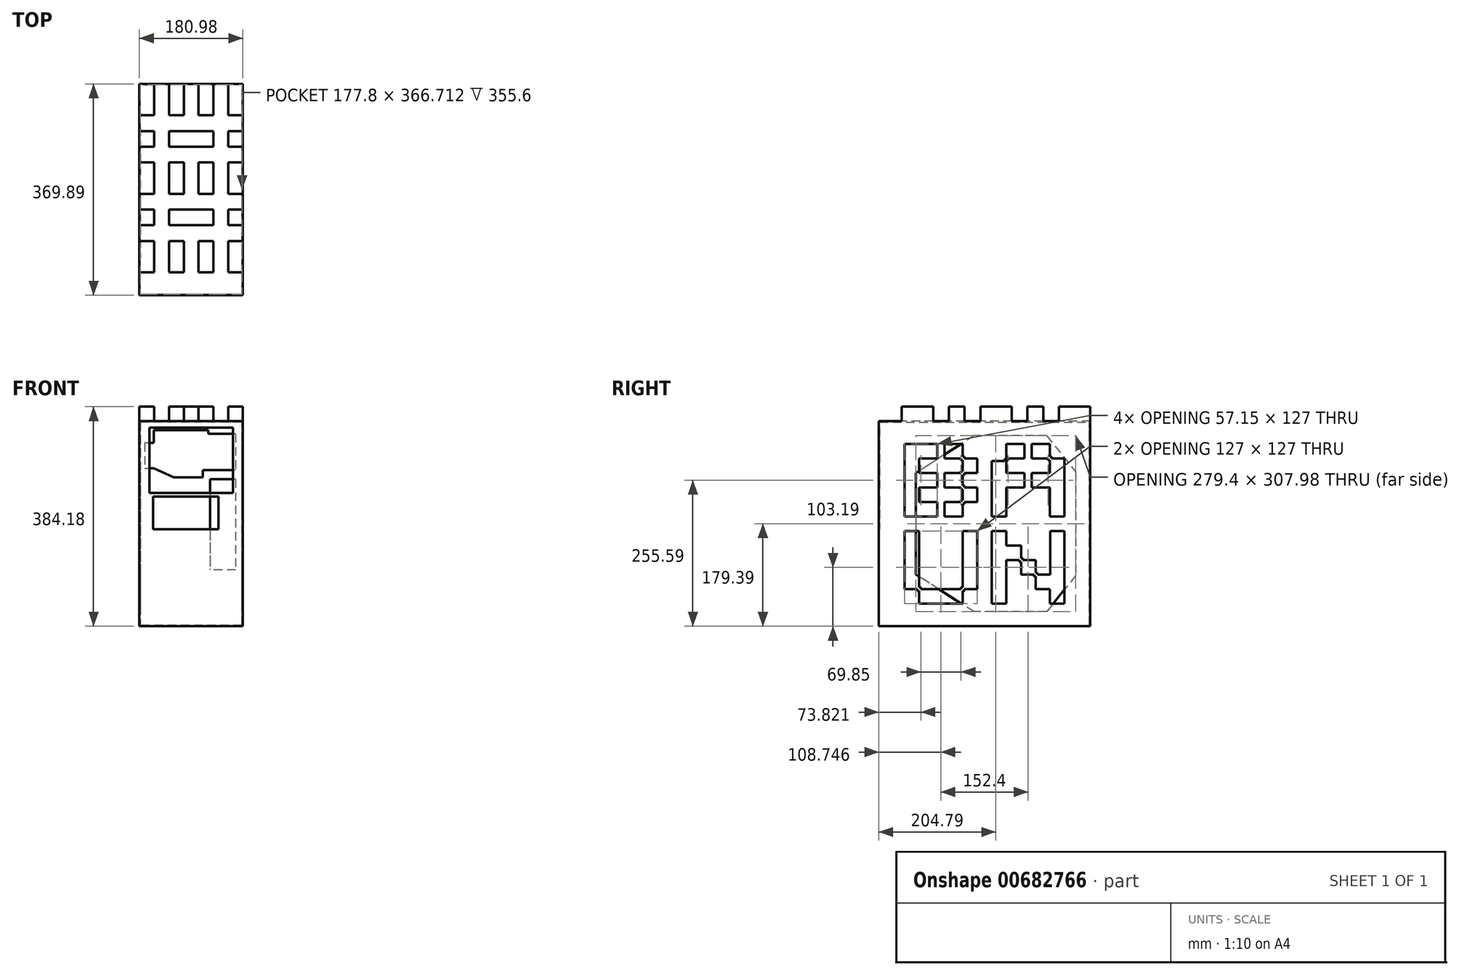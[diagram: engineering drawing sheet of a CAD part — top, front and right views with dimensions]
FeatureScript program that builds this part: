
annotation { "Feature Type Name" : "Feature", "Feature Type Description" : "" }
export const myFeature = defineFeature(function(context is Context, id is Id, definition is map)
    precondition{}
    {
        {
            var Q0;
            Q0=qCreatedBy(makeId("Front.planeOp"),FACE);
            var sketch = newSketch(context, id + "F0", { "sketchPlane" : qUnion([Q0])});
            skLineSegment(sketch, "E0", {"start": v(-88.9, -177.8) * mm, "end": v(88.9, -177.8) * mm});
            skLineSegment(sketch, "E1", {"start": v(88.9, -177.8) * mm, "end": v(88.9, 177.8) * mm});
            skLineSegment(sketch, "E2", {"start": v(88.9, 177.8) * mm, "end": v(-88.9, 177.8) * mm});
            skLineSegment(sketch, "E3", {"start": v(-88.9, -177.8) * mm, "end": v(-88.9, 177.8) * mm});
            skSolve(sketch);
        }
        {
            var Q0;
            Q0 = qSketchRegion(id + "F0", true);
            extrude(context, id + "F1", {"entities" : qUnion([Q0]), "depth" : 1.59 * mm, "offsetDistance" : 25.4 * mm});
        }
        {
            var Q0;
            Q0=makeQuery(id+"F1.opExtrude","CAP_FACE",FACE,{"disambiguationData":[OSD([sQuery(id+"F0.wireOp",EDGE,"E0"),sQuery(id+"F0.wireOp",EDGE,"E1"),sQuery(id+"F0.wireOp",EDGE,"E2"),sQuery(id+"F0.wireOp",EDGE,"E3")])],"isStart":false});
            var sketch = newSketch(context, id + "F2", { "sketchPlane" : qUnion([Q0])});
            skLineSegment(sketch, "E4", {"start": v(-88.9, 168.28) * mm, "end": v(-73.03, 168.28) * mm, "construction": true});
            skLineSegment(sketch, "E5", {"start": v(-73.03, 168.28) * mm, "end": v(73.03, 168.28) * mm});
            skLineSegment(sketch, "E6", {"start": v(73.03, 168.28) * mm, "end": v(73.03, 53.98) * mm});
            skLineSegment(sketch, "E7", {"start": v(73.03, 53.98) * mm, "end": v(-73.03, 53.98) * mm});
            skLineSegment(sketch, "E8", {"start": v(-73.03, 168.28) * mm, "end": v(-73.03, 53.98) * mm});
            skLineSegment(sketch, "E9", {"start": v(-66.67, 53.97) * mm, "end": v(-66.67, 47.62) * mm});
            skLineSegment(sketch, "E10", {"start": v(-66.67, 47.62) * mm, "end": v(47.62, 47.63) * mm});
            skLineSegment(sketch, "E11", {"start": v(47.62, 47.63) * mm, "end": v(47.62, -9.52) * mm});
            skLineSegment(sketch, "E12", {"start": v(47.62, -9.52) * mm, "end": v(-66.67, -9.52) * mm});
            skLineSegment(sketch, "E13", {"start": v(-66.67, 47.62) * mm, "end": v(-66.67, -9.52) * mm});
            skSolve(sketch);
        }
        {
            var Q0;
            Q0 = qSketchRegion(id + "F2", true);
            extrude(context, id + "F3", {"entities" : qUnion([Q0]), "operationType" : NewBodyOperationType.REMOVE, "endBound" : BoundingType.THROUGH_ALL, "oppositeDirection" : true, "depth" : 25.4 * mm, "offsetDistance" : 25.4 * mm});
        }
        {
            var Q0;
            Q0=makeQuery(id+"F1.opExtrude","SWEPT_FACE",FACE,{"disambiguationData":[OSD([sQuery(id+"F0.wireOp",EDGE,"E3")])]});
            var sketch = newSketch(context, id + "F4", { "sketchPlane" : qUnion([Q0])});
            skLineSegment(sketch, "E14", {"start": v(1.59, 177.8) * mm, "end": v(-366.71, 177.8) * mm});
            skLineSegment(sketch, "E15", {"start": v(-366.71, 177.8) * mm, "end": v(-366.71, -177.8) * mm});
            skLineSegment(sketch, "E16", {"start": v(1.59, -177.8) * mm, "end": v(-366.71, -177.8) * mm});
            skLineSegment(sketch, "E17", {"start": v(1.59, -177.8) * mm, "end": v(1.59, 177.8) * mm});
            skSolve(sketch);
        }
        {
            var Q0;
            Q0 = qSketchRegion(id + "F4", true);
            extrude(context, id + "F5", {"entities" : qUnion([Q0]), "operationType" : NewBodyOperationType.ADD, "depth" : 1.59 * mm, "offsetDistance" : 25.4 * mm});
        }
        {
            var Q0;
            Q0=makeQuery(id+"F1.opExtrude","SWEPT_FACE",FACE,{"disambiguationData":[OSD([sQuery(id+"F0.wireOp",EDGE,"E1")])]});
            var sketch = newSketch(context, id + "F6", { "sketchPlane" : qUnion([Q0])});
            skLineSegment(sketch, "E18", {"start": v(-1.59, -177.8) * mm, "end": v(366.71, -177.8) * mm});
            skLineSegment(sketch, "E19", {"start": v(-1.59, 177.8) * mm, "end": v(-1.59, -177.8) * mm});
            skLineSegment(sketch, "E20", {"start": v(366.71, -177.8) * mm, "end": v(366.71, 177.8) * mm});
            skLineSegment(sketch, "E21", {"start": v(-1.59, 177.8) * mm, "end": v(366.71, 177.8) * mm});
            skSolve(sketch);
        }
        {
            var Q0;
            Q0 = qSketchRegion(id + "F6", true);
            extrude(context, id + "F7", {"entities" : qUnion([Q0]), "operationType" : NewBodyOperationType.ADD, "depth" : 1.59 * mm, "offsetDistance" : 25.4 * mm});
        }
        {
            var Q0;
            Q0=makeQuery(id+"F7.boolean.opBoolean","MERGE",FACE,{"derivedFrom":[makeQuery(id+"F5.boolean.opBoolean","MERGE",FACE,{"derivedFrom":[makeQuery(id+"F1.opExtrude","SWEPT_FACE",FACE,{"disambiguationData":[OSD([sQuery(id+"F0.wireOp",EDGE,"E2")])]}),makeQuery(id+"F5.opExtrude","SWEPT_FACE",FACE,{"disambiguationData":[OSD([sQuery(id+"F4.wireOp",EDGE,"E14")])]})]}),makeQuery(id+"F7.opExtrude","SWEPT_FACE",FACE,{"disambiguationData":[OSD([sQuery(id+"F6.wireOp",EDGE,"E21")])]})]});
            var sketch = newSketch(context, id + "F8", { "sketchPlane" : qUnion([Q0])});
            skLineSegment(sketch, "E22", {"start": v(90.49, 366.71) * mm, "end": v(-90.49, 366.71) * mm});
            skLineSegment(sketch, "E23", {"start": v(-90.49, 366.71) * mm, "end": v(-90.49, -1.59) * mm});
            skLineSegment(sketch, "E24", {"start": v(-90.49, -1.59) * mm, "end": v(90.49, -1.59) * mm});
            skLineSegment(sketch, "E25", {"start": v(90.49, -1.59) * mm, "end": v(90.49, 366.71) * mm});
            skSolve(sketch);
        }
        {
            var Q0;
            Q0 = qSketchRegion(id + "F8", true);
            extrude(context, id + "F9", {"entities" : qUnion([Q0]), "operationType" : NewBodyOperationType.ADD, "depth" : 1.59 * mm, "offsetDistance" : 25.4 * mm});
        }
        {
            var Q0;
            Q0=makeQuery(id+"F7.boolean.opBoolean","MERGE",FACE,{"derivedFrom":[makeQuery(id+"F5.boolean.opBoolean","MERGE",FACE,{"derivedFrom":[makeQuery(id+"F1.opExtrude","SWEPT_FACE",FACE,{"disambiguationData":[OSD([sQuery(id+"F0.wireOp",EDGE,"E0")])]}),makeQuery(id+"F5.opExtrude","SWEPT_FACE",FACE,{"disambiguationData":[OSD([sQuery(id+"F4.wireOp",EDGE,"E16")])]})]}),makeQuery(id+"F7.opExtrude","SWEPT_FACE",FACE,{"disambiguationData":[OSD([sQuery(id+"F6.wireOp",EDGE,"E18")])]})]});
            var sketch = newSketch(context, id + "F10", { "sketchPlane" : qUnion([Q0])});
            skLineSegment(sketch, "E26", {"start": v(-90.49, 1.59) * mm, "end": v(90.49, 1.59) * mm});
            skLineSegment(sketch, "E27", {"start": v(90.49, 1.59) * mm, "end": v(90.49, -366.71) * mm});
            skLineSegment(sketch, "E28", {"start": v(90.49, -366.71) * mm, "end": v(-90.49, -366.71) * mm});
            skLineSegment(sketch, "E29", {"start": v(-90.49, -366.71) * mm, "end": v(-90.49, 1.59) * mm});
            skSolve(sketch);
        }
        {
            var Q0;
            Q0 = qSketchRegion(id + "F10", true);
            extrude(context, id + "F11", {"entities" : qUnion([Q0]), "operationType" : NewBodyOperationType.ADD, "depth" : 1.59 * mm, "offsetDistance" : 25.4 * mm});
        }
        {
            var Q0;
            Q0=makeQuery(id+"F11.boolean.opBoolean","MERGE",FACE,{"derivedFrom":[makeQuery(id+"F9.boolean.opBoolean","MERGE",FACE,{"derivedFrom":[makeQuery(id+"F5.opExtrude","SWEPT_FACE",FACE,{"disambiguationData":[OSD([sQuery(id+"F4.wireOp",EDGE,"E15")])]}),makeQuery(id+"F7.opExtrude","SWEPT_FACE",FACE,{"disambiguationData":[OSD([sQuery(id+"F6.wireOp",EDGE,"E20")])]}),makeQuery(id+"F9.opExtrude","SWEPT_FACE",FACE,{"disambiguationData":[OSD([sQuery(id+"F8.wireOp",EDGE,"E22")])]})]}),makeQuery(id+"F11.opExtrude","SWEPT_FACE",FACE,{"disambiguationData":[OSD([sQuery(id+"F10.wireOp",EDGE,"E28")])]})]});
            var sketch = newSketch(context, id + "F12", { "sketchPlane" : qUnion([Q0])});
            skLineSegment(sketch, "E30", {"start": v(90.49, -179.39) * mm, "end": v(-90.49, -179.39) * mm});
            skLineSegment(sketch, "E31", {"start": v(-90.49, -179.39) * mm, "end": v(-90.49, 179.39) * mm});
            skLineSegment(sketch, "E32", {"start": v(-90.49, 179.39) * mm, "end": v(90.49, 179.39) * mm});
            skLineSegment(sketch, "E33", {"start": v(90.49, 179.39) * mm, "end": v(90.49, -179.39) * mm});
            skSolve(sketch);
        }
        {
            var Q0;
            Q0 = qSketchRegion(id + "F12", true);
            extrude(context, id + "F13", {"entities" : qUnion([Q0]), "operationType" : NewBodyOperationType.ADD, "depth" : 1.59 * mm, "offsetDistance" : 25.4 * mm});
        }
        {
            var Q0;
            Q0=makeQuery(id+"F13.opExtrude","CAP_FACE",FACE,{"disambiguationData":[OSD([sQuery(id+"F12.wireOp",EDGE,"E30"),sQuery(id+"F12.wireOp",EDGE,"E31"),sQuery(id+"F12.wireOp",EDGE,"E32"),sQuery(id+"F12.wireOp",EDGE,"E33")])],"isStart":false});
            var sketch = newSketch(context, id + "F14", { "sketchPlane" : qUnion([Q0])});
            skLineSegment(sketch, "E34", {"start": v(-90.49, 157.16) * mm, "end": v(-77.79, 157.16) * mm, "construction": true});
            skLineSegment(sketch, "E35", {"start": v(-77.79, 157.16) * mm, "end": v(-77.79, 93.66) * mm});
            skLineSegment(sketch, "E36", {"start": v(-77.79, 93.66) * mm, "end": v(-20.64, 93.66) * mm});
            skLineSegment(sketch, "E37", {"start": v(-77.79, 157.16) * mm, "end": v(-30.16, 157.16) * mm});
            skLineSegment(sketch, "E38", {"start": v(-30.16, 157.16) * mm, "end": v(-30.16, 163.51) * mm});
            skLineSegment(sketch, "E39", {"start": v(-30.16, 163.51) * mm, "end": v(65.09, 163.51) * mm});
            skLineSegment(sketch, "E40", {"start": v(65.09, 163.51) * mm, "end": v(65.09, 141.29) * mm});
            skLineSegment(sketch, "E41", {"start": v(65.09, 141.29) * mm, "end": v(80.96, 141.29) * mm});
            skLineSegment(sketch, "E42", {"start": v(80.96, 141.29) * mm, "end": v(80.96, 96.84) * mm});
            skLineSegment(sketch, "E43", {"start": v(80.96, 96.84) * mm, "end": v(65.09, 96.84) * mm});
            skLineSegment(sketch, "E44", {"start": v(-20.64, 93.66) * mm, "end": v(-20.64, 80.96) * mm});
            skLineSegment(sketch, "E45", {"start": v(-20.64, 80.96) * mm, "end": v(30.16, 80.96) * mm});
            skLineSegment(sketch, "E46", {"start": v(30.16, 80.96) * mm, "end": v(65.09, 96.84) * mm});
            skSolve(sketch);
        }
        {
            var Q0;
            Q0 = qSketchRegion(id + "F14", true);
            extrude(context, id + "F15", {"entities" : qUnion([Q0]), "operationType" : NewBodyOperationType.REMOVE, "oppositeDirection" : true, "depth" : 25.4 * mm, "offsetDistance" : 25.4 * mm});
        }
        {
            var Q0;
            Q0=makeQuery(id+"F13.opExtrude","CAP_FACE",FACE,{"disambiguationData":[OSD([sQuery(id+"F12.wireOp",EDGE,"E30"),sQuery(id+"F12.wireOp",EDGE,"E31"),sQuery(id+"F12.wireOp",EDGE,"E32"),sQuery(id+"F12.wireOp",EDGE,"E33")])],"isStart":false});
            var sketch = newSketch(context, id + "F16", { "sketchPlane" : qUnion([Q0])});
            skLineSegment(sketch, "E47", {"start": v(-90.49, 77.79) * mm, "end": v(-77.79, 77.79) * mm, "construction": true});
            skLineSegment(sketch, "E48", {"start": v(-77.79, 77.79) * mm, "end": v(-33.34, 77.79) * mm});
            skLineSegment(sketch, "E49", {"start": v(-77.79, 77.79) * mm, "end": v(-77.79, -80.96) * mm});
            skLineSegment(sketch, "E50", {"start": v(-77.79, -80.96) * mm, "end": v(-33.34, -80.96) * mm});
            skLineSegment(sketch, "E51", {"start": v(-33.34, 77.79) * mm, "end": v(-33.34, -80.96) * mm});
            skSolve(sketch);
        }
        {
            var Q0;
            Q0 = qSketchRegion(id + "F16", true);
            extrude(context, id + "F17", {"entities" : qUnion([Q0]), "operationType" : NewBodyOperationType.REMOVE, "oppositeDirection" : true, "depth" : 25.4 * mm, "offsetDistance" : 25.4 * mm});
        }
        {
            var Q0;
            Q0=makeQuery(id+"F13.boolean.opBoolean","MERGE",FACE,{"derivedFrom":[makeQuery(id+"F11.boolean.opBoolean","MERGE",FACE,{"derivedFrom":[makeQuery(id+"F9.boolean.opBoolean","MERGE",FACE,{"derivedFrom":[makeQuery(id+"F7.opExtrude","CAP_FACE",FACE,{"disambiguationData":[OSD([sQuery(id+"F6.wireOp",EDGE,"E18"),sQuery(id+"F6.wireOp",EDGE,"E19"),sQuery(id+"F6.wireOp",EDGE,"E20"),sQuery(id+"F6.wireOp",EDGE,"E21")])],"isStart":false}),makeQuery(id+"F9.opExtrude","SWEPT_FACE",FACE,{"disambiguationData":[OSD([sQuery(id+"F8.wireOp",EDGE,"E25")])]})]}),makeQuery(id+"F11.opExtrude","SWEPT_FACE",FACE,{"disambiguationData":[OSD([sQuery(id+"F10.wireOp",EDGE,"E27")])]})]}),makeQuery(id+"F13.opExtrude","SWEPT_FACE",FACE,{"disambiguationData":[OSD([sQuery(id+"F12.wireOp",EDGE,"E31")])]})]});
            var sketch = newSketch(context, id + "F18", { "sketchPlane" : qUnion([Q0])});
            skLineSegment(sketch, "E52", {"start": v(43.66, 139.7) * mm, "end": v(43.66, 114.3) * mm});
            skLineSegment(sketch, "E53", {"start": v(43.66, 139.7) * mm, "end": v(69.06, 139.7) * mm});
            skLineSegment(sketch, "E54", {"start": v(323.06, -139.7) * mm, "end": v(297.66, -139.7) * mm});
            skLineSegment(sketch, "E55", {"start": v(69.06, 139.7) * mm, "end": v(94.46, 139.7) * mm});
            skLineSegment(sketch, "E56", {"start": v(94.46, 139.7) * mm, "end": v(100.8, 139.7) * mm});
            skLineSegment(sketch, "E57", {"start": v(119.86, 139.7) * mm, "end": v(145.26, 139.7) * mm});
            skLineSegment(sketch, "E58", {"start": v(221.46, 139.7) * mm, "end": v(246.86, 139.7) * mm});
            skLineSegment(sketch, "E59", {"start": v(246.86, 139.7) * mm, "end": v(253.2, 139.7) * mm});
            skLineSegment(sketch, "E60", {"start": v(272.26, 139.7) * mm, "end": v(297.66, 139.7) * mm});
            skLineSegment(sketch, "E61", {"start": v(43.66, 114.3) * mm, "end": v(43.66, 88.9) * mm});
            skLineSegment(sketch, "E62", {"start": v(43.66, 88.9) * mm, "end": v(43.66, 63.5) * mm});
            skLineSegment(sketch, "E63", {"start": v(43.66, 63.5) * mm, "end": v(43.66, 38.1) * mm});
            skLineSegment(sketch, "E64", {"start": v(43.66, 38.1) * mm, "end": v(43.66, 12.7) * mm});
            skLineSegment(sketch, "E65", {"start": v(43.66, 12.7) * mm, "end": v(43.66, -12.7) * mm, "construction": true});
            skLineSegment(sketch, "E66", {"start": v(43.66, -12.7) * mm, "end": v(43.66, -38.1) * mm});
            skLineSegment(sketch, "E67", {"start": v(43.66, -38.1) * mm, "end": v(43.66, -63.5) * mm});
            skLineSegment(sketch, "E68", {"start": v(43.66, -63.5) * mm, "end": v(43.66, -88.9) * mm});
            skLineSegment(sketch, "E69", {"start": v(43.66, -88.9) * mm, "end": v(43.66, -114.3) * mm});
            skLineSegment(sketch, "E70", {"start": v(43.66, -12.7) * mm, "end": v(69.06, -12.7) * mm});
            skLineSegment(sketch, "E71", {"start": v(43.66, -114.3) * mm, "end": v(65.88, -114.3) * mm});
            skLineSegment(sketch, "E72", {"start": v(323.06, 114.3) * mm, "end": v(323.06, 88.9) * mm});
            skLineSegment(sketch, "E73", {"start": v(272.26, 139.7) * mm, "end": v(272.26, 114.3) * mm, "construction": true});
            skLineSegment(sketch, "E74", {"start": v(246.86, 139.7) * mm, "end": v(246.86, 114.3) * mm, "construction": true});
            skLineSegment(sketch, "E75", {"start": v(196.06, 109.54) * mm, "end": v(196.06, 12.7) * mm});
            skLineSegment(sketch, "E76", {"start": v(170.66, 114.3) * mm, "end": v(170.66, 88.9) * mm});
            skLineSegment(sketch, "E77", {"start": v(145.26, 139.7) * mm, "end": v(145.26, 117.48) * mm});
            skLineSegment(sketch, "E78", {"start": v(119.86, 139.7) * mm, "end": v(119.86, 114.3) * mm, "construction": true});
            skLineSegment(sketch, "E79", {"start": v(94.46, 139.7) * mm, "end": v(94.46, 114.3) * mm, "construction": true});
            skLineSegment(sketch, "E80.trimOffspring", {"start": v(94.46, 88.9) * mm, "end": v(94.46, 63.5) * mm, "construction": true});
            skLineSegment(sketch, "E81.trimOffspring", {"start": v(119.86, 88.9) * mm, "end": v(119.86, 63.5) * mm, "construction": true});
            skLineSegment(sketch, "E82.trimOffspring", {"start": v(94.46, 38.1) * mm, "end": v(94.46, 12.7) * mm, "construction": true});
            skLineSegment(sketch, "E83.trimOffspring", {"start": v(119.86, 38.1) * mm, "end": v(119.86, 12.7) * mm, "construction": true});
            skLineSegment(sketch, "E84.trimOffspring", {"start": v(170.66, 63.5) * mm, "end": v(170.66, 38.1) * mm});
            skLineSegment(sketch, "E85.trimOffspring", {"start": v(196.06, 12.7) * mm, "end": v(221.46, 12.7) * mm});
            skLineSegment(sketch, "E86.trimOffspring", {"start": v(170.66, -12.7) * mm, "end": v(170.66, -114.3) * mm});
            skLineSegment(sketch, "E87.trimOffspring", {"start": v(196.06, -12.7) * mm, "end": v(196.06, -139.7) * mm});
            skLineSegment(sketch, "E88.trimOffspring", {"start": v(196.06, -12.7) * mm, "end": v(221.46, -12.7) * mm});
            skLineSegment(sketch, "E89.trimOffspring", {"start": v(145.26, -12.7) * mm, "end": v(145.26, -111.13) * mm});
            skLineSegment(sketch, "E90.trimOffspring", {"start": v(69.06, -12.7) * mm, "end": v(69.06, -111.13) * mm});
            skLineSegment(sketch, "E91", {"start": v(145.26, 139.7) * mm, "end": v(221.46, 139.7) * mm, "construction": true});
            skPoint(sketch, "E92.orphan", {"position": v(323.06, 139.7) * mm});
            skLineSegment(sketch, "E93.trimOffspring", {"start": v(297.66, 12.7) * mm, "end": v(323.06, 12.7) * mm});
            skLineSegment(sketch, "E94.trimOffspring", {"start": v(298.12, -12.7) * mm, "end": v(323.06, -12.7) * mm});
            skLineSegment(sketch, "E95.trimOffspring", {"start": v(145.26, -139.7) * mm, "end": v(69.06, -139.7) * mm});
            skLineSegment(sketch, "E96.trimOffspring", {"start": v(221.46, -139.7) * mm, "end": v(196.06, -139.7) * mm});
            skPoint(sketch, "E97.end.orphan", {"position": v(43.66, -139.7) * mm});
            skLineSegment(sketch, "E98.trimOffspring", {"start": v(145.26, -12.7) * mm, "end": v(170.66, -12.7) * mm});
            skLineSegment(sketch, "E99", {"start": v(43.66, -139.7) * mm, "end": v(43.66, -114.3) * mm, "construction": true});
            skLineSegment(sketch, "E100", {"start": v(43.66, -139.7) * mm, "end": v(69.06, -139.7) * mm, "construction": true});
            skLineSegment(sketch, "E101", {"start": v(145.26, -139.7) * mm, "end": v(196.06, -139.7) * mm, "construction": true});
            skLineSegment(sketch, "E102", {"start": v(221.46, -139.7) * mm, "end": v(297.66, -139.7) * mm, "construction": true});
            skLineSegment(sketch, "E103.trimOffspring", {"start": v(323.06, -12.7) * mm, "end": v(323.06, -139.7) * mm});
            skLineSegment(sketch, "E104", {"start": v(323.06, -12.7) * mm, "end": v(323.06, 12.7) * mm, "construction": true});
            skLineSegment(sketch, "E105", {"start": v(323.06, 114.3) * mm, "end": v(323.06, 139.7) * mm, "construction": true});
            skLineSegment(sketch, "E106", {"start": v(297.66, 139.7) * mm, "end": v(323.06, 139.7) * mm, "construction": true});
            skLineSegment(sketch, "E107", {"start": v(183.36, 139.7) * mm, "end": v(183.36, 101.44) * mm, "construction": true});
            skLineSegment(sketch, "E108", {"start": v(43.66, 0) * mm, "end": v(83.28, 0) * mm, "construction": true});
            skLineSegment(sketch, "E109.trimOffspring", {"start": v(246.86, 88.9) * mm, "end": v(246.86, 63.5) * mm, "construction": true});
            skLineSegment(sketch, "E110.trimOffspring", {"start": v(272.26, 88.9) * mm, "end": v(272.26, 63.5) * mm, "construction": true});
            skLineSegment(sketch, "E111", {"start": v(119.86, 114.3) * mm, "end": v(142.08, 114.3) * mm});
            skLineSegment(sketch, "E112", {"start": v(119.86, 114.3) * mm, "end": v(113.5, 114.3) * mm});
            skLineSegment(sketch, "E113", {"start": v(94.46, 114.3) * mm, "end": v(69.06, 114.3) * mm});
            skLineSegment(sketch, "E114", {"start": v(69.06, 88.9) * mm, "end": v(94.46, 88.9) * mm});
            skLineSegment(sketch, "E115", {"start": v(94.46, 88.9) * mm, "end": v(100.8, 88.9) * mm});
            skLineSegment(sketch, "E116", {"start": v(119.86, 88.9) * mm, "end": v(142.08, 88.9) * mm});
            skLineSegment(sketch, "E117", {"start": v(170.66, 114.3) * mm, "end": v(148.43, 114.3) * mm});
            skLineSegment(sketch, "E118", {"start": v(170.66, 88.9) * mm, "end": v(148.43, 88.9) * mm});
            skLineSegment(sketch, "E119", {"start": v(170.66, 63.5) * mm, "end": v(148.43, 63.5) * mm});
            skLineSegment(sketch, "E120", {"start": v(170.66, 38.1) * mm, "end": v(148.43, 38.1) * mm});
            skLineSegment(sketch, "E121", {"start": v(142.08, 38.1) * mm, "end": v(119.86, 38.1) * mm});
            skLineSegment(sketch, "E122", {"start": v(119.86, 38.1) * mm, "end": v(113.5, 38.1) * mm});
            skLineSegment(sketch, "E123", {"start": v(94.46, 38.1) * mm, "end": v(69.06, 38.1) * mm});
            skLineSegment(sketch, "E124", {"start": v(69.06, 63.5) * mm, "end": v(94.46, 63.5) * mm});
            skLineSegment(sketch, "E125", {"start": v(94.46, 63.5) * mm, "end": v(100.8, 63.5) * mm});
            skLineSegment(sketch, "E126", {"start": v(119.86, 63.5) * mm, "end": v(142.08, 63.5) * mm});
            skLineSegment(sketch, "E127", {"start": v(69.06, 88.9) * mm, "end": v(69.06, 114.3) * mm});
            skLineSegment(sketch, "E128", {"start": v(69.06, 38.1) * mm, "end": v(69.06, 63.5) * mm});
            skLineSegment(sketch, "E129", {"start": v(272.26, 88.9) * mm, "end": v(297.66, 88.9) * mm});
            skLineSegment(sketch, "E130", {"start": v(272.26, 88.9) * mm, "end": v(265.9, 88.9) * mm});
            skLineSegment(sketch, "E131", {"start": v(246.86, 88.9) * mm, "end": v(221.46, 88.9) * mm});
            skLineSegment(sketch, "E132", {"start": v(221.46, 139.7) * mm, "end": v(221.46, 112.71) * mm});
            skLineSegment(sketch, "E133", {"start": v(221.46, 111.13) * mm, "end": v(221.46, 88.9) * mm});
            skLineSegment(sketch, "E134", {"start": v(221.46, 63.5) * mm, "end": v(221.46, 38.1) * mm});
            skLineSegment(sketch, "E135", {"start": v(221.46, 38.1) * mm, "end": v(221.46, 12.7) * mm});
            skLineSegment(sketch, "E136", {"start": v(323.06, 114.3) * mm, "end": v(300.83, 114.3) * mm});
            skLineSegment(sketch, "E137", {"start": v(294.48, 114.3) * mm, "end": v(272.26, 114.3) * mm});
            skLineSegment(sketch, "E138", {"start": v(246.86, 114.3) * mm, "end": v(253.2, 114.3) * mm});
            skLineSegment(sketch, "E139", {"start": v(246.86, 114.3) * mm, "end": v(224.63, 114.3) * mm});
            skLineSegment(sketch, "E140", {"start": v(196.06, 109.54) * mm, "end": v(218.28, 109.54) * mm});
            skLineSegment(sketch, "E141", {"start": v(272.26, 63.5) * mm, "end": v(297.66, 63.5) * mm});
            skLineSegment(sketch, "E142", {"start": v(272.26, 63.5) * mm, "end": v(265.9, 63.5) * mm});
            skLineSegment(sketch, "E143", {"start": v(221.46, 63.5) * mm, "end": v(246.86, 63.5) * mm});
            skLineSegment(sketch, "E144", {"start": v(297.66, 111.12) * mm, "end": v(297.66, 88.9) * mm});
            skLineSegment(sketch, "E145", {"start": v(297.66, 63.5) * mm, "end": v(297.66, 38.1) * mm});
            skLineSegment(sketch, "E146", {"start": v(297.66, 12.7) * mm, "end": v(297.66, 38.1) * mm});
            skLineSegment(sketch, "E147", {"start": v(247.32, -38.1) * mm, "end": v(221.46, -38.1) * mm});
            skLineSegment(sketch, "E148", {"start": v(272.72, -63.5) * mm, "end": v(250.5, -63.5) * mm});
            skLineSegment(sketch, "E149", {"start": v(221.46, -12.7) * mm, "end": v(221.46, -38.1) * mm});
            skLineSegment(sketch, "E150", {"start": v(221.46, -63.5) * mm, "end": v(221.46, -88.9) * mm});
            skLineSegment(sketch, "E151", {"start": v(221.46, -114.3) * mm, "end": v(221.46, -88.9) * mm});
            skLineSegment(sketch, "E152", {"start": v(247.32, -88.9) * mm, "end": v(269.54, -88.9) * mm});
            skLineSegment(sketch, "E153", {"start": v(272.72, -114.33) * mm, "end": v(297.66, -114.33) * mm});
            skLineSegment(sketch, "E154", {"start": v(298.12, -12.7) * mm, "end": v(298.12, -38.1) * mm});
            skLineSegment(sketch, "E155", {"start": v(298.12, -63.5) * mm, "end": v(298.12, -38.1) * mm});
            skLineSegment(sketch, "E156", {"start": v(298.12, -88.9) * mm, "end": v(298.12, -63.5) * mm});
            skLineSegment(sketch, "E157", {"start": v(297.66, -139.7) * mm, "end": v(297.66, -114.33) * mm});
            skLineSegment(sketch, "E158", {"start": v(221.46, -139.7) * mm, "end": v(221.46, -114.3) * mm});
            skLineSegment(sketch, "E159", {"start": v(253.2, 63.5) * mm, "end": v(246.86, 63.5) * mm});
            skLineSegment(sketch, "E160", {"start": v(253.2, 63.5) * mm, "end": v(253.2, 88.9) * mm});
            skLineSegment(sketch, "E161.trimOffspring", {"start": v(253.2, 88.9) * mm, "end": v(246.86, 88.9) * mm});
            skLineSegment(sketch, "E162.trimOffspring", {"start": v(253.2, 114.3) * mm, "end": v(253.2, 139.7) * mm});
            skLineSegment(sketch, "E163.trimOffspring", {"start": v(265.9, 114.3) * mm, "end": v(265.9, 139.7) * mm});
            skLineSegment(sketch, "E164.trimOffspring", {"start": v(265.9, 139.7) * mm, "end": v(272.26, 139.7) * mm});
            skLineSegment(sketch, "E165.trimOffspring", {"start": v(265.9, 114.3) * mm, "end": v(272.26, 114.3) * mm});
            skLineSegment(sketch, "E166", {"start": v(145.26, 12.7) * mm, "end": v(119.86, 12.7) * mm});
            skLineSegment(sketch, "E167", {"start": v(119.86, 12.7) * mm, "end": v(113.5, 12.7) * mm});
            skLineSegment(sketch, "E168", {"start": v(94.46, 12.7) * mm, "end": v(69.06, 12.7) * mm});
            skLineSegment(sketch, "E169", {"start": v(69.06, 12.7) * mm, "end": v(43.66, 12.7) * mm});
            skLineSegment(sketch, "E170", {"start": v(100.8, 12.7) * mm, "end": v(94.46, 12.7) * mm});
            skLineSegment(sketch, "E171", {"start": v(100.8, 12.7) * mm, "end": v(100.8, 38.1) * mm});
            skLineSegment(sketch, "E172", {"start": v(113.5, 12.7) * mm, "end": v(113.5, 38.1) * mm});
            skLineSegment(sketch, "E173.trimOffspring", {"start": v(100.8, 63.5) * mm, "end": v(100.8, 88.9) * mm});
            skLineSegment(sketch, "E174.trimOffspring", {"start": v(113.5, 63.5) * mm, "end": v(113.5, 88.9) * mm});
            skLineSegment(sketch, "E175.trimOffspring", {"start": v(100.8, 38.1) * mm, "end": v(94.46, 38.1) * mm});
            skLineSegment(sketch, "E176.trimOffspring", {"start": v(113.5, 63.5) * mm, "end": v(119.86, 63.5) * mm});
            skLineSegment(sketch, "E177.trimOffspring", {"start": v(113.5, 88.9) * mm, "end": v(119.86, 88.9) * mm});
            skLineSegment(sketch, "E178.trimOffspring", {"start": v(113.5, 114.3) * mm, "end": v(113.5, 139.7) * mm});
            skLineSegment(sketch, "E179.trimOffspring", {"start": v(100.8, 114.3) * mm, "end": v(94.46, 114.3) * mm});
            skLineSegment(sketch, "E180.trimOffspring", {"start": v(100.8, 114.3) * mm, "end": v(100.8, 139.7) * mm});
            skLineSegment(sketch, "E181.trimOffspring", {"start": v(113.5, 139.7) * mm, "end": v(119.86, 139.7) * mm});
            skLineSegment(sketch, "E182", {"start": v(265.9, 63.5) * mm, "end": v(265.9, 88.9) * mm});
            skLineSegment(sketch, "E183", {"start": v(272.72, -114.33) * mm, "end": v(272.72, -92.08) * mm});
            skLineSegment(sketch, "E184", {"start": v(272.72, -63.5) * mm, "end": v(272.72, -85.73) * mm});
            skLineSegment(sketch, "E185", {"start": v(247.32, -88.9) * mm, "end": v(247.32, -66.67) * mm});
            skLineSegment(sketch, "E186", {"start": v(221.46, -63.5) * mm, "end": v(244.14, -63.5) * mm});
            skLineSegment(sketch, "E187", {"start": v(247.32, -38.1) * mm, "end": v(247.32, -60.33) * mm});
            skLineSegment(sketch, "E188", {"start": v(275.9, -88.9) * mm, "end": v(298.12, -88.9) * mm});
            skLineSegment(sketch, "E189", {"start": v(275.9, -88.9) * mm, "end": v(275.9, -85.73) * mm});
            skLineSegment(sketch, "E190", {"start": v(272.72, -92.08) * mm, "end": v(269.54, -92.08) * mm});
            skLineSegment(sketch, "E191", {"start": v(244.14, -63.5) * mm, "end": v(244.14, -66.67) * mm});
            skLineSegment(sketch, "E192", {"start": v(247.32, -60.33) * mm, "end": v(250.5, -60.33) * mm});
            skLineSegment(sketch, "E193", {"start": v(244.14, -66.67) * mm, "end": v(247.32, -66.67) * mm});
            skLineSegment(sketch, "E194", {"start": v(250.5, -60.33) * mm, "end": v(250.5, -63.5) * mm});
            skLineSegment(sketch, "E195", {"start": v(275.9, -85.73) * mm, "end": v(272.72, -85.73) * mm});
            skLineSegment(sketch, "E196", {"start": v(269.54, -92.08) * mm, "end": v(269.54, -88.9) * mm});
            skLineSegment(sketch, "E197", {"start": v(142.08, 114.3) * mm, "end": v(142.08, 111.13) * mm});
            skLineSegment(sketch, "E198", {"start": v(142.08, 111.13) * mm, "end": v(145.26, 111.13) * mm});
            skLineSegment(sketch, "E199", {"start": v(145.26, 117.48) * mm, "end": v(148.43, 117.48) * mm});
            skLineSegment(sketch, "E200", {"start": v(148.43, 117.48) * mm, "end": v(148.43, 114.3) * mm});
            skLineSegment(sketch, "E201", {"start": v(145.26, 85.73) * mm, "end": v(148.43, 85.73) * mm});
            skLineSegment(sketch, "E202", {"start": v(148.43, 85.73) * mm, "end": v(148.43, 88.9) * mm});
            skLineSegment(sketch, "E203", {"start": v(142.08, 88.9) * mm, "end": v(142.08, 92.08) * mm});
            skLineSegment(sketch, "E204", {"start": v(142.08, 92.08) * mm, "end": v(145.26, 92.08) * mm});
            skLineSegment(sketch, "E205.trimOffspring", {"start": v(145.26, 111.13) * mm, "end": v(145.26, 92.08) * mm});
            skLineSegment(sketch, "E206.trimOffspring", {"start": v(145.26, 85.73) * mm, "end": v(145.26, 66.68) * mm});
            skLineSegment(sketch, "E207", {"start": v(145.26, 66.68) * mm, "end": v(148.43, 66.68) * mm});
            skLineSegment(sketch, "E208", {"start": v(148.43, 66.68) * mm, "end": v(148.43, 63.5) * mm});
            skLineSegment(sketch, "E209", {"start": v(145.26, 60.33) * mm, "end": v(142.08, 60.33) * mm});
            skLineSegment(sketch, "E210", {"start": v(142.08, 60.33) * mm, "end": v(142.08, 63.5) * mm});
            skLineSegment(sketch, "E211", {"start": v(145.26, 41.27) * mm, "end": v(142.08, 41.27) * mm});
            skLineSegment(sketch, "E212", {"start": v(142.08, 41.27) * mm, "end": v(142.08, 38.1) * mm});
            skLineSegment(sketch, "E213", {"start": v(145.26, 34.92) * mm, "end": v(148.43, 34.92) * mm});
            skLineSegment(sketch, "E214", {"start": v(148.43, 34.92) * mm, "end": v(148.43, 38.1) * mm});
            skLineSegment(sketch, "E215.trimOffspring", {"start": v(145.26, 34.92) * mm, "end": v(145.26, 12.7) * mm});
            skLineSegment(sketch, "E216.trimOffspring", {"start": v(145.26, 60.33) * mm, "end": v(145.26, 41.27) * mm});
            skLineSegment(sketch, "E217", {"start": v(221.46, 111.12) * mm, "end": v(224.63, 111.12) * mm});
            skLineSegment(sketch, "E218", {"start": v(224.63, 111.12) * mm, "end": v(224.63, 114.3) * mm});
            skLineSegment(sketch, "E219", {"start": v(218.28, 109.54) * mm, "end": v(218.28, 112.71) * mm});
            skLineSegment(sketch, "E220", {"start": v(218.28, 112.71) * mm, "end": v(221.46, 112.71) * mm});
            skLineSegment(sketch, "E221", {"start": v(294.48, 114.3) * mm, "end": v(294.48, 111.12) * mm});
            skLineSegment(sketch, "E222", {"start": v(294.48, 111.12) * mm, "end": v(297.66, 111.12) * mm});
            skLineSegment(sketch, "E223", {"start": v(297.66, 117.47) * mm, "end": v(300.83, 117.47) * mm});
            skLineSegment(sketch, "E224", {"start": v(300.83, 117.47) * mm, "end": v(300.83, 114.3) * mm});
            skLineSegment(sketch, "E225", {"start": v(253.2, 139.7) * mm, "end": v(265.9, 139.7) * mm, "construction": true});
            skLineSegment(sketch, "E226", {"start": v(113.5, 139.7) * mm, "end": v(100.8, 139.7) * mm, "construction": true});
            skLineSegment(sketch, "E227", {"start": v(297.66, 139.7) * mm, "end": v(297.66, 117.47) * mm});
            skLineSegment(sketch, "E228", {"start": v(323.06, 88.9) * mm, "end": v(323.06, 63.5) * mm});
            skLineSegment(sketch, "E229", {"start": v(323.06, 63.5) * mm, "end": v(323.06, 38.1) * mm});
            skLineSegment(sketch, "E230", {"start": v(323.06, 38.1) * mm, "end": v(323.06, 12.7) * mm});
            skPoint(sketch, "E231.orphan", {"position": v(297.66, 114.3) * mm});
            skLineSegment(sketch, "E232", {"start": v(148.43, -114.3) * mm, "end": v(148.43, -117.48) * mm});
            skLineSegment(sketch, "E233", {"start": v(148.43, -117.48) * mm, "end": v(145.26, -117.48) * mm});
            skLineSegment(sketch, "E234", {"start": v(142.08, -114.3) * mm, "end": v(142.08, -111.13) * mm});
            skLineSegment(sketch, "E235", {"start": v(142.08, -111.13) * mm, "end": v(145.26, -111.13) * mm});
            skLineSegment(sketch, "E236.trimOffspring", {"start": v(148.43, -114.3) * mm, "end": v(170.66, -114.3) * mm});
            skLineSegment(sketch, "E237.trimOffspring", {"start": v(145.26, -117.48) * mm, "end": v(145.26, -139.7) * mm});
            skLineSegment(sketch, "E238", {"start": v(72.23, -114.3) * mm, "end": v(72.23, -111.13) * mm});
            skLineSegment(sketch, "E239", {"start": v(72.23, -111.13) * mm, "end": v(69.06, -111.13) * mm});
            skLineSegment(sketch, "E240", {"start": v(65.88, -114.3) * mm, "end": v(65.88, -117.48) * mm});
            skLineSegment(sketch, "E241", {"start": v(65.88, -117.48) * mm, "end": v(69.06, -117.48) * mm});
            skLineSegment(sketch, "E242.trimOffspring", {"start": v(69.06, -117.48) * mm, "end": v(69.06, -139.7) * mm});
            skLineSegment(sketch, "E243.trimOffspring", {"start": v(72.23, -114.3) * mm, "end": v(142.08, -114.3) * mm});
            skSolve(sketch);
        }
        {
            var Q0;
            Q0 = qSketchRegion(id + "F18", true);
            extrude(context, id + "F19", {"entities" : qUnion([Q0]), "operationType" : NewBodyOperationType.REMOVE, "oppositeDirection" : true, "depth" : 25.4 * mm, "offsetDistance" : 25.4 * mm});
        }
        {
            var Q0;
            Q0=makeQuery(id+"F13.boolean.opBoolean","MERGE",FACE,{"derivedFrom":[makeQuery(id+"F9.opExtrude","CAP_FACE",FACE,{"disambiguationData":[OSD([sQuery(id+"F8.wireOp",EDGE,"E22"),sQuery(id+"F8.wireOp",EDGE,"E23"),sQuery(id+"F8.wireOp",EDGE,"E24"),sQuery(id+"F8.wireOp",EDGE,"E25")])],"isStart":false}),makeQuery(id+"F13.opExtrude","SWEPT_FACE",FACE,{"disambiguationData":[OSD([sQuery(id+"F12.wireOp",EDGE,"E32")])]})]});
            var sketch = newSketch(context, id + "F20", { "sketchPlane" : qUnion([Q0])});
            skLineSegment(sketch, "E244", {"start": v(-90.49, 368.3) * mm, "end": v(-64.63, 368.3) * mm});
            skLineSegment(sketch, "E245", {"start": v(-38.78, 368.3) * mm, "end": v(-12.93, 368.3) * mm});
            skLineSegment(sketch, "E246", {"start": v(12.93, 368.3) * mm, "end": v(38.78, 368.3) * mm});
            skLineSegment(sketch, "E247", {"start": v(64.63, 368.3) * mm, "end": v(90.49, 368.3) * mm});
            skLineSegment(sketch, "E248", {"start": v(90.49, 368.3) * mm, "end": v(90.49, 340.82) * mm});
            skLineSegment(sketch, "E249", {"start": v(90.49, 340.82) * mm, "end": v(90.49, 313.35) * mm});
            skLineSegment(sketch, "E250", {"start": v(90.49, 285.87) * mm, "end": v(90.49, 258.4) * mm});
            skLineSegment(sketch, "E251", {"start": v(90.49, 230.92) * mm, "end": v(90.49, 203.44) * mm});
            skLineSegment(sketch, "E252", {"start": v(90.49, 203.44) * mm, "end": v(90.49, 175.97) * mm});
            skLineSegment(sketch, "E253", {"start": v(90.49, 175.97) * mm, "end": v(90.49, 148.5) * mm});
            skLineSegment(sketch, "E254", {"start": v(90.49, 148.5) * mm, "end": v(90.49, 121.02) * mm});
            skLineSegment(sketch, "E255", {"start": v(90.49, 121.02) * mm, "end": v(90.49, 93.54) * mm});
            skLineSegment(sketch, "E256", {"start": v(90.49, 93.54) * mm, "end": v(90.49, 66.06) * mm});
            skLineSegment(sketch, "E257", {"start": v(90.49, 66.06) * mm, "end": v(90.49, 38.59) * mm});
            skLineSegment(sketch, "E258", {"start": v(90.49, 38.59) * mm, "end": v(64.63, 38.59) * mm});
            skLineSegment(sketch, "E259", {"start": v(90.49, 66.06) * mm, "end": v(64.63, 66.06) * mm, "construction": true});
            skLineSegment(sketch, "E260", {"start": v(90.49, 93.54) * mm, "end": v(64.63, 93.54) * mm});
            skLineSegment(sketch, "E261", {"start": v(90.49, 121.02) * mm, "end": v(64.63, 121.02) * mm});
            skLineSegment(sketch, "E262", {"start": v(90.49, 148.5) * mm, "end": v(64.63, 148.5) * mm});
            skLineSegment(sketch, "E263", {"start": v(90.49, 175.97) * mm, "end": v(64.63, 175.97) * mm});
            skLineSegment(sketch, "E264", {"start": v(90.49, 203.44) * mm, "end": v(64.63, 203.44) * mm, "construction": true});
            skLineSegment(sketch, "E265", {"start": v(90.49, 230.92) * mm, "end": v(64.63, 230.92) * mm});
            skLineSegment(sketch, "E266", {"start": v(90.49, 258.4) * mm, "end": v(64.63, 258.4) * mm});
            skLineSegment(sketch, "E267", {"start": v(90.49, 285.87) * mm, "end": v(64.63, 285.87) * mm});
            skLineSegment(sketch, "E268", {"start": v(90.49, 313.35) * mm, "end": v(64.63, 313.35) * mm});
            skLineSegment(sketch, "E269", {"start": v(90.49, 340.82) * mm, "end": v(64.63, 340.82) * mm, "construction": true});
            skLineSegment(sketch, "E270", {"start": v(64.63, 368.3) * mm, "end": v(64.63, 340.82) * mm});
            skLineSegment(sketch, "E271", {"start": v(64.63, 340.82) * mm, "end": v(64.63, 313.35) * mm});
            skLineSegment(sketch, "E272", {"start": v(64.63, 285.87) * mm, "end": v(64.63, 258.4) * mm});
            skLineSegment(sketch, "E273", {"start": v(64.63, 230.92) * mm, "end": v(64.63, 203.44) * mm});
            skLineSegment(sketch, "E274", {"start": v(64.63, 203.44) * mm, "end": v(64.63, 175.97) * mm});
            skLineSegment(sketch, "E275", {"start": v(64.63, 148.5) * mm, "end": v(64.63, 121.02) * mm});
            skLineSegment(sketch, "E276", {"start": v(64.63, 93.54) * mm, "end": v(64.63, 66.06) * mm});
            skLineSegment(sketch, "E277", {"start": v(64.63, 66.06) * mm, "end": v(64.63, 38.59) * mm});
            skLineSegment(sketch, "E278", {"start": v(38.78, 368.3) * mm, "end": v(38.78, 340.82) * mm});
            skLineSegment(sketch, "E279", {"start": v(38.78, 340.82) * mm, "end": v(38.78, 313.35) * mm});
            skLineSegment(sketch, "E280", {"start": v(38.78, 285.87) * mm, "end": v(38.78, 258.4) * mm});
            skLineSegment(sketch, "E281", {"start": v(38.78, 230.92) * mm, "end": v(38.78, 203.44) * mm});
            skLineSegment(sketch, "E282", {"start": v(38.78, 203.44) * mm, "end": v(38.78, 175.97) * mm});
            skLineSegment(sketch, "E283", {"start": v(38.78, 148.5) * mm, "end": v(38.78, 121.02) * mm});
            skLineSegment(sketch, "E284", {"start": v(38.78, 93.54) * mm, "end": v(38.78, 66.06) * mm});
            skLineSegment(sketch, "E285", {"start": v(38.78, 66.06) * mm, "end": v(38.78, 38.59) * mm});
            skLineSegment(sketch, "E286", {"start": v(12.93, 368.3) * mm, "end": v(12.93, 340.82) * mm});
            skLineSegment(sketch, "E287", {"start": v(12.93, 340.82) * mm, "end": v(12.93, 313.35) * mm});
            skLineSegment(sketch, "E288", {"start": v(12.93, 285.87) * mm, "end": v(12.93, 258.4) * mm, "construction": true});
            skLineSegment(sketch, "E289", {"start": v(12.93, 230.92) * mm, "end": v(12.93, 203.44) * mm});
            skLineSegment(sketch, "E290", {"start": v(12.93, 203.44) * mm, "end": v(12.93, 175.97) * mm});
            skLineSegment(sketch, "E291", {"start": v(12.93, 148.5) * mm, "end": v(12.93, 121.02) * mm, "construction": true});
            skLineSegment(sketch, "E292", {"start": v(12.93, 93.54) * mm, "end": v(12.93, 66.06) * mm});
            skLineSegment(sketch, "E293", {"start": v(12.93, 66.06) * mm, "end": v(12.93, 38.59) * mm});
            skLineSegment(sketch, "E294", {"start": v(-12.93, 368.3) * mm, "end": v(-12.93, 340.82) * mm});
            skLineSegment(sketch, "E295", {"start": v(-12.93, 340.82) * mm, "end": v(-12.93, 313.35) * mm});
            skLineSegment(sketch, "E296", {"start": v(-12.93, 285.87) * mm, "end": v(-12.93, 258.4) * mm, "construction": true});
            skLineSegment(sketch, "E297", {"start": v(-12.93, 230.92) * mm, "end": v(-12.93, 203.44) * mm});
            skLineSegment(sketch, "E298", {"start": v(-12.93, 203.44) * mm, "end": v(-12.93, 175.97) * mm});
            skLineSegment(sketch, "E299", {"start": v(-12.93, 148.5) * mm, "end": v(-12.93, 121.02) * mm, "construction": true});
            skLineSegment(sketch, "E300", {"start": v(-12.93, 93.54) * mm, "end": v(-12.93, 66.06) * mm});
            skLineSegment(sketch, "E301", {"start": v(-12.93, 66.06) * mm, "end": v(-12.93, 38.59) * mm});
            skLineSegment(sketch, "E302", {"start": v(-38.78, 340.82) * mm, "end": v(-38.78, 313.35) * mm});
            skLineSegment(sketch, "E303", {"start": v(-38.78, 285.87) * mm, "end": v(-38.78, 258.4) * mm});
            skLineSegment(sketch, "E304", {"start": v(-38.78, 230.92) * mm, "end": v(-38.78, 203.44) * mm});
            skLineSegment(sketch, "E305", {"start": v(-38.78, 203.44) * mm, "end": v(-38.78, 175.97) * mm});
            skLineSegment(sketch, "E306", {"start": v(-38.78, 148.5) * mm, "end": v(-38.78, 121.02) * mm});
            skLineSegment(sketch, "E307", {"start": v(-38.78, 93.54) * mm, "end": v(-38.78, 66.06) * mm});
            skLineSegment(sketch, "E308", {"start": v(-38.78, 66.06) * mm, "end": v(-38.78, 38.59) * mm});
            skLineSegment(sketch, "E309", {"start": v(-64.63, 368.3) * mm, "end": v(-64.63, 340.82) * mm});
            skLineSegment(sketch, "E310", {"start": v(-64.63, 340.82) * mm, "end": v(-64.63, 313.35) * mm});
            skLineSegment(sketch, "E311", {"start": v(-64.63, 285.87) * mm, "end": v(-64.63, 258.4) * mm});
            skLineSegment(sketch, "E312", {"start": v(-64.63, 230.92) * mm, "end": v(-64.63, 203.44) * mm});
            skLineSegment(sketch, "E313", {"start": v(-64.63, 203.44) * mm, "end": v(-64.63, 175.97) * mm});
            skLineSegment(sketch, "E314", {"start": v(-64.63, 148.5) * mm, "end": v(-64.63, 121.02) * mm});
            skLineSegment(sketch, "E315", {"start": v(-64.63, 93.54) * mm, "end": v(-64.63, 66.06) * mm});
            skLineSegment(sketch, "E316", {"start": v(-64.63, 66.06) * mm, "end": v(-64.63, 38.59) * mm});
            skLineSegment(sketch, "E317", {"start": v(-38.78, 368.3) * mm, "end": v(-38.78, 340.82) * mm});
            skLineSegment(sketch, "E318.trimOffspring", {"start": v(-64.63, 340.82) * mm, "end": v(-90.49, 340.82) * mm, "construction": true});
            skLineSegment(sketch, "E319.trimOffspring", {"start": v(-12.93, 340.82) * mm, "end": v(-38.78, 340.82) * mm, "construction": true});
            skLineSegment(sketch, "E320.trimOffspring", {"start": v(38.78, 340.82) * mm, "end": v(12.93, 340.82) * mm, "construction": true});
            skLineSegment(sketch, "E321.trimOffspring", {"start": v(38.78, 313.35) * mm, "end": v(12.93, 313.35) * mm});
            skLineSegment(sketch, "E322.trimOffspring", {"start": v(-12.93, 313.35) * mm, "end": v(-38.78, 313.35) * mm});
            skLineSegment(sketch, "E323.trimOffspring", {"start": v(-64.63, 313.35) * mm, "end": v(-90.49, 313.35) * mm});
            skLineSegment(sketch, "E324", {"start": v(-90.49, 368.3) * mm, "end": v(-90.49, 340.82) * mm});
            skLineSegment(sketch, "E325", {"start": v(-90.49, 313.35) * mm, "end": v(-90.49, 340.82) * mm});
            skLineSegment(sketch, "E326", {"start": v(-90.49, 285.87) * mm, "end": v(-90.49, 258.4) * mm});
            skLineSegment(sketch, "E327", {"start": v(-90.49, 230.92) * mm, "end": v(-90.49, 203.44) * mm});
            skLineSegment(sketch, "E328", {"start": v(-90.49, 203.44) * mm, "end": v(-90.49, 175.97) * mm});
            skLineSegment(sketch, "E329", {"start": v(-90.49, 148.5) * mm, "end": v(-90.49, 121.02) * mm});
            skLineSegment(sketch, "E330", {"start": v(-90.49, 93.54) * mm, "end": v(-90.49, 66.06) * mm});
            skLineSegment(sketch, "E331", {"start": v(-90.49, 66.06) * mm, "end": v(-90.49, 38.59) * mm});
            skLineSegment(sketch, "E332.trimOffspring", {"start": v(38.78, 285.87) * mm, "end": v(-38.78, 285.87) * mm});
            skLineSegment(sketch, "E333.trimOffspring", {"start": v(-64.63, 285.87) * mm, "end": v(-90.49, 285.87) * mm});
            skLineSegment(sketch, "E334.trimOffspring", {"start": v(38.78, 258.4) * mm, "end": v(-38.78, 258.4) * mm});
            skLineSegment(sketch, "E335.trimOffspring", {"start": v(-64.63, 258.4) * mm, "end": v(-90.49, 258.4) * mm});
            skLineSegment(sketch, "E336.trimOffspring", {"start": v(38.78, 230.92) * mm, "end": v(12.93, 230.92) * mm});
            skLineSegment(sketch, "E337.trimOffspring", {"start": v(38.78, 203.44) * mm, "end": v(12.93, 203.44) * mm, "construction": true});
            skLineSegment(sketch, "E338.trimOffspring", {"start": v(38.78, 175.97) * mm, "end": v(12.93, 175.97) * mm});
            skLineSegment(sketch, "E339.trimOffspring", {"start": v(38.78, 148.5) * mm, "end": v(-38.78, 148.5) * mm});
            skLineSegment(sketch, "E340.trimOffspring", {"start": v(38.78, 121.02) * mm, "end": v(-38.78, 121.02) * mm});
            skLineSegment(sketch, "E341.trimOffspring", {"start": v(38.78, 93.54) * mm, "end": v(12.93, 93.54) * mm});
            skLineSegment(sketch, "E342.trimOffspring", {"start": v(38.78, 66.06) * mm, "end": v(12.93, 66.06) * mm, "construction": true});
            skLineSegment(sketch, "E343.trimOffspring", {"start": v(38.78, 38.59) * mm, "end": v(12.93, 38.59) * mm});
            skLineSegment(sketch, "E344.trimOffspring", {"start": v(-12.93, 230.92) * mm, "end": v(-38.78, 230.92) * mm});
            skLineSegment(sketch, "E345.trimOffspring", {"start": v(-12.93, 203.44) * mm, "end": v(-38.78, 203.44) * mm, "construction": true});
            skLineSegment(sketch, "E346.trimOffspring", {"start": v(-12.93, 175.97) * mm, "end": v(-38.78, 175.97) * mm});
            skLineSegment(sketch, "E347.trimOffspring", {"start": v(-64.63, 175.97) * mm, "end": v(-90.49, 175.97) * mm});
            skLineSegment(sketch, "E348.trimOffspring", {"start": v(-64.63, 203.44) * mm, "end": v(-90.49, 203.44) * mm, "construction": true});
            skLineSegment(sketch, "E349.trimOffspring", {"start": v(-64.63, 230.92) * mm, "end": v(-90.49, 230.92) * mm});
            skLineSegment(sketch, "E350.trimOffspring", {"start": v(-64.63, 121.02) * mm, "end": v(-90.49, 121.02) * mm});
            skLineSegment(sketch, "E351.trimOffspring", {"start": v(-64.63, 148.5) * mm, "end": v(-90.49, 148.5) * mm});
            skLineSegment(sketch, "E352.trimOffspring", {"start": v(-12.93, 66.06) * mm, "end": v(-38.78, 66.06) * mm, "construction": true});
            skLineSegment(sketch, "E353.trimOffspring", {"start": v(-12.93, 38.59) * mm, "end": v(-38.78, 38.59) * mm});
            skLineSegment(sketch, "E354.trimOffspring", {"start": v(-64.63, 38.59) * mm, "end": v(-90.49, 38.59) * mm});
            skLineSegment(sketch, "E355.trimOffspring", {"start": v(-64.63, 66.06) * mm, "end": v(-90.49, 66.06) * mm, "construction": true});
            skLineSegment(sketch, "E356.trimOffspring", {"start": v(-64.63, 93.54) * mm, "end": v(-90.49, 93.54) * mm});
            skLineSegment(sketch, "E357.trimOffspring", {"start": v(-12.93, 93.54) * mm, "end": v(-38.78, 93.54) * mm});
            skSolve(sketch);
        }
        {
            var Q0;
            Q0 = qSketchRegion(id + "F20", true);
            extrude(context, id + "F21", {"entities" : qUnion([Q0]), "operationType" : NewBodyOperationType.ADD, "depth" : 25.4 * mm, "offsetDistance" : 25.4 * mm});
        }
        {
            var Q0;
            Q0=makeQuery(id+"F21.boolean.opBoolean","MERGE",FACE,{"derivedFrom":[makeQuery(id+"F13.boolean.opBoolean","MERGE",FACE,{"derivedFrom":[makeQuery(id+"F11.boolean.opBoolean","MERGE",FACE,{"derivedFrom":[makeQuery(id+"F9.boolean.opBoolean","MERGE",FACE,{"derivedFrom":[makeQuery(id+"F5.opExtrude","CAP_FACE",FACE,{"disambiguationData":[OSD([sQuery(id+"F4.wireOp",EDGE,"E14"),sQuery(id+"F4.wireOp",EDGE,"E15"),sQuery(id+"F4.wireOp",EDGE,"E16"),sQuery(id+"F4.wireOp",EDGE,"E17")])],"isStart":false}),makeQuery(id+"F9.opExtrude","SWEPT_FACE",FACE,{"disambiguationData":[OSD([sQuery(id+"F8.wireOp",EDGE,"E23")])]})]}),makeQuery(id+"F11.opExtrude","SWEPT_FACE",FACE,{"disambiguationData":[OSD([sQuery(id+"F10.wireOp",EDGE,"E29")])]})]}),makeQuery(id+"F13.opExtrude","SWEPT_FACE",FACE,{"disambiguationData":[OSD([sQuery(id+"F12.wireOp",EDGE,"E33")])]})]}),makeQuery(id+"F21.opExtrude","SWEPT_FACE",FACE,{"disambiguationData":[OSD([sQuery(id+"F20.wireOp",EDGE,"E324"),sQuery(id+"F20.wireOp",EDGE,"E325")])]}),makeQuery(id+"F21.opExtrude","SWEPT_FACE",FACE,{"disambiguationData":[OSD([sQuery(id+"F20.wireOp",EDGE,"E326")])]}),makeQuery(id+"F21.opExtrude","SWEPT_FACE",FACE,{"disambiguationData":[OSD([sQuery(id+"F20.wireOp",EDGE,"E327"),sQuery(id+"F20.wireOp",EDGE,"E328")])]}),makeQuery(id+"F21.opExtrude","SWEPT_FACE",FACE,{"disambiguationData":[OSD([sQuery(id+"F20.wireOp",EDGE,"E329")])]}),makeQuery(id+"F21.opExtrude","SWEPT_FACE",FACE,{"disambiguationData":[OSD([sQuery(id+"F20.wireOp",EDGE,"E330"),sQuery(id+"F20.wireOp",EDGE,"E331")])]})]});
            var sketch = newSketch(context, id + "F22", { "sketchPlane" : qUnion([Q0])});
            skLineSegment(sketch, "E358", {"start": v(-183.36, 165.1) * mm, "end": v(-183.36, 137.13) * mm, "construction": true});
            skLineSegment(sketch, "E359", {"start": v(-348.46, 0) * mm, "end": v(-287.45, 0) * mm, "construction": true});
            skLineSegment(sketch, "E360", {"start": v(-342.9, 90.49) * mm, "end": v(-342.9, -90.49) * mm});
            skLineSegment(sketch, "E361", {"start": v(-292.1, 153.99) * mm, "end": v(-165.1, 153.99) * mm});
            skLineSegment(sketch, "E362", {"start": v(-292.1, 153.99) * mm, "end": v(-342.9, 90.49) * mm});
            skLineSegment(sketch, "E363", {"start": v(-292.1, -153.99) * mm, "end": v(-165.1, -153.99) * mm});
            skLineSegment(sketch, "E364", {"start": v(-342.9, -90.49) * mm, "end": v(-292.1, -153.99) * mm});
            skPoint(sketch, "E365.bottom.start.orphan", {"position": v(-348.46, 165.1) * mm});
            skLineSegment(sketch, "E366", {"start": v(-63.5, 88.9) * mm, "end": v(-63.5, -88.9) * mm});
            skLineSegment(sketch, "E367", {"start": v(-165.1, -153.99) * mm, "end": v(-63.5, -88.9) * mm});
            skLineSegment(sketch, "E368", {"start": v(-165.1, 153.99) * mm, "end": v(-63.5, 88.9) * mm});
            skPoint(sketch, "E369.end.orphan", {"position": v(-18.26, 165.1) * mm});
            skSolve(sketch);
        }
        {
            var Q0;
            Q0 = qSketchRegion(id + "F22", true);
            extrude(context, id + "F23", {"entities" : qUnion([Q0]), "operationType" : NewBodyOperationType.REMOVE, "oppositeDirection" : true, "depth" : 25.4 * mm, "offsetDistance" : 25.4 * mm});
        }
    });
